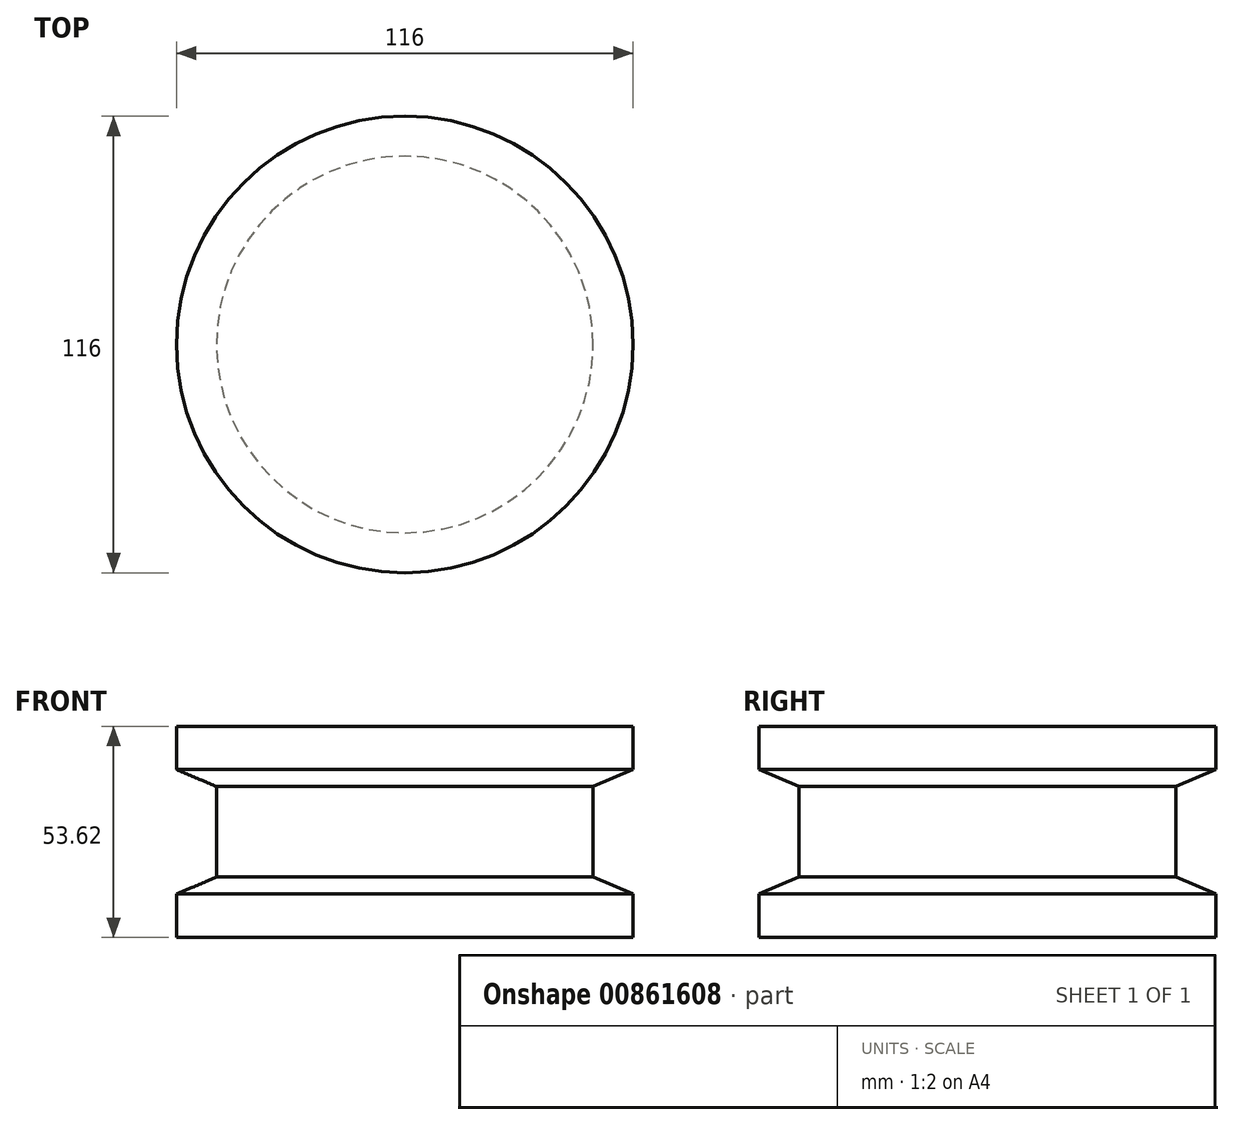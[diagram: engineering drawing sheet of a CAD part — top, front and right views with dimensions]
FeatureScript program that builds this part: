
annotation { "Feature Type Name" : "Feature", "Feature Type Description" : "" }
export const myFeature = defineFeature(function(context is Context, id is Id, definition is map)
    precondition{}
    {
        {
            var Q0;
            Q0=qCreatedBy(makeId("Right.planeOp"),FACE);
            var sketch = newSketch(context, id + "F0", { "sketchPlane" : qUnion([Q0])});
            skLineSegment(sketch, "E0.bottom", {"start": v(-108.22, -87.78) * mm, "end": v(-166.22, -87.78) * mm});
            skLineSegment(sketch, "E0.top", {"start": v(-108.22, -34.16) * mm, "end": v(-166.22, -34.16) * mm});
            skLineSegment(sketch, "E0.left", {"start": v(-108.22, -87.78) * mm, "end": v(-108.22, -34.16) * mm});
            skPoint(sketch, "E0.middle", {"position": v(-137.22, -60.97) * mm});
            skLineSegment(sketch, "E1", {"start": v(-166.22, -34.16) * mm, "end": v(-166.22, -45.16) * mm});
            skLineSegment(sketch, "E2", {"start": v(-166.22, -45.16) * mm, "end": v(-156.06, -49.47) * mm});
            skLineSegment(sketch, "E3", {"start": v(-156.06, -49.47) * mm, "end": v(-156.06, -72.47) * mm});
            skLineSegment(sketch, "E4", {"start": v(-156.06, -72.47) * mm, "end": v(-166.22, -76.78) * mm});
            skLineSegment(sketch, "E5", {"start": v(-166.22, -76.78) * mm, "end": v(-166.22, -87.78) * mm});
            skSolve(sketch);
        }
        {
            var Q0;
            Q0=makeQuery(id+"F0.imprint","IMPRINT",FACE,{"disambiguationData":[TD([[makeQuery(id+"F0.imprint","IMPRINT",EDGE,{"derivedFrom":sQuery(id+"F0.wireOp",EDGE,"E0.bottom")}),-1.0]])]});
            var Q1;
            Q1=sQuery(id+"F0.wireOp",EDGE,"E0.left");
            revolve(context, id + "F1", {"surfaceOperationType" : NewSurfaceOperationType.NEW, "entities" : qUnion([Q0]), "axis" : qUnion([Q1]), "revolveType" : RevolveType.FULL});
        }
    });
